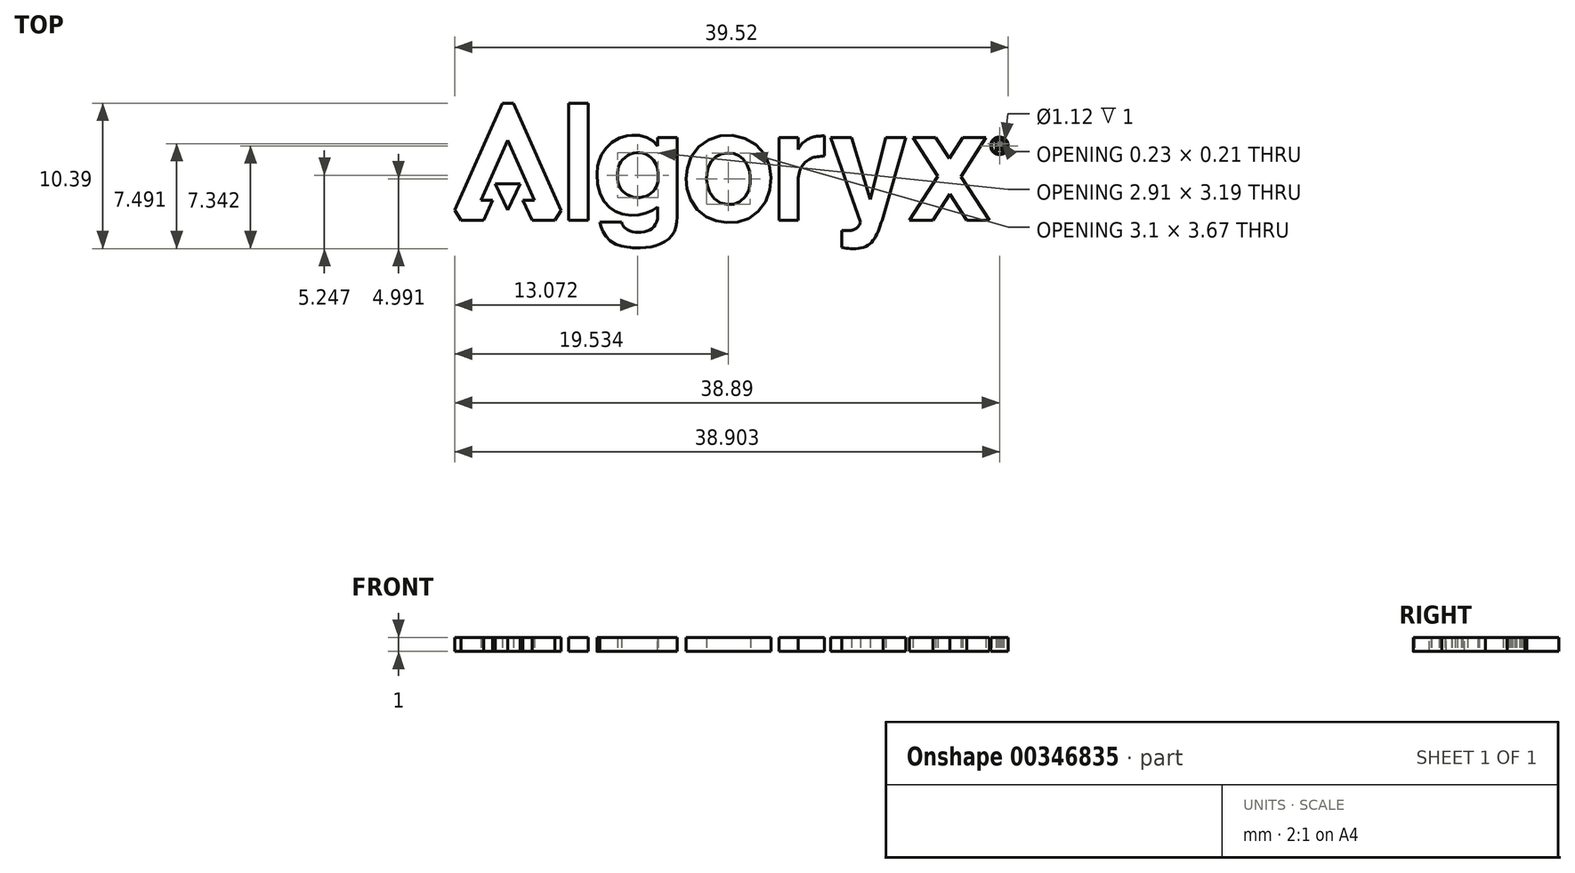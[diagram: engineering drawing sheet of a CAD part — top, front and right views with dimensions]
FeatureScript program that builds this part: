
annotation { "Feature Type Name" : "Feature", "Feature Type Description" : "" }
export const myFeature = defineFeature(function(context is Context, id is Id, definition is map)
    precondition{}
    {
        {
            var Q0;
            Q0=qCreatedBy(makeId("Top.planeOp"),FACE);
            var sketch = newSketch(context, id + "F0", { "sketchPlane" : qUnion([Q0])});
            skLineSegment(sketch, "E0", {"start": v(-19.75, -2.44) * mm, "end": v(-16.35, 5.19) * mm});
            skLineSegment(sketch, "E1", {"start": v(-16.35, 5.19) * mm, "end": v(-15.56, 5.19) * mm});
            skLineSegment(sketch, "E2", {"start": v(-15.56, 5.19) * mm, "end": v(-12.16, -2.46) * mm});
            skLineSegment(sketch, "E3", {"start": v(-12.16, -2.46) * mm, "end": v(-12.6, -3.16) * mm});
            skLineSegment(sketch, "E4", {"start": v(-12.6, -3.16) * mm, "end": v(-14.23, -3.16) * mm});
            skLineSegment(sketch, "E5", {"start": v(-14.23, -3.16) * mm, "end": v(-14.87, -1.75) * mm});
            skLineSegment(sketch, "E6", {"start": v(-14.87, -1.75) * mm, "end": v(-14.04, -1.75) * mm});
            skLineSegment(sketch, "E7", {"start": v(-14.04, -1.75) * mm, "end": v(-15.95, 2.54) * mm});
            skLineSegment(sketch, "E8", {"start": v(-15.95, 2.54) * mm, "end": v(-17.87, -1.75) * mm});
            skLineSegment(sketch, "E9", {"start": v(-17.87, -1.75) * mm, "end": v(-17.03, -1.75) * mm});
            skLineSegment(sketch, "E10", {"start": v(-17.03, -1.75) * mm, "end": v(-17.7, -3.16) * mm});
            skLineSegment(sketch, "E11", {"start": v(-17.7, -3.16) * mm, "end": v(-19.3, -3.16) * mm});
            skLineSegment(sketch, "E12", {"start": v(-19.3, -3.16) * mm, "end": v(-19.75, -2.44) * mm});
            skLineSegment(sketch, "E13", {"start": v(-16.84, -0.58) * mm, "end": v(-15.08, -0.58) * mm});
            skLineSegment(sketch, "E14", {"start": v(-15.08, -0.58) * mm, "end": v(-15.96, -2.45) * mm});
            skLineSegment(sketch, "E15", {"start": v(-15.96, -2.45) * mm, "end": v(-16.84, -0.58) * mm});
            skLineSegment(sketch, "E16.bottom", {"start": v(-11.62, 5.19) * mm, "end": v(-10.2, 5.19) * mm});
            skLineSegment(sketch, "E16.top", {"start": v(-11.62, -3.16) * mm, "end": v(-10.2, -3.16) * mm});
            skLineSegment(sketch, "E16.left", {"start": v(-11.62, 5.19) * mm, "end": v(-11.62, -3.16) * mm});
            skLineSegment(sketch, "E16.right", {"start": v(-10.2, 5.19) * mm, "end": v(-10.2, -3.16) * mm});
            skLineSegment(sketch, "E17", {"start": v(-3.86, 2.72) * mm, "end": v(-3.86, -2.9) * mm});
            skFitSpline(sketch, "E18", {"points": [v(-3.86, -2.9) * mm, v(-4.12, -4.08) * mm, v(-4.9, -4.78) * mm, v(-6, -5.1) * mm, v(-7.01, -5.14) * mm, v(-7.23, -5.12) * mm, v(-8.58, -4.7) * mm, v(-9.33, -3.57) * mm, v(-9.4, -3.29) * mm], "startDerivative": vector(-0.36, -9.23) * mm, "endDerivative": vector(-0.73, 3.2) * mm});
            skLineSegment(sketch, "E19", {"start": v(-9.4, -3.29) * mm, "end": v(-7.85, -3.29) * mm});
            skFitSpline(sketch, "E20", {"points": [v(-7.85, -3.29) * mm, v(-7.73, -3.56) * mm, v(-7.48, -3.82) * mm, v(-6.92, -4.02) * mm, v(-6.2, -4) * mm, v(-5.63, -3.75) * mm, v(-5.3, -3.17) * mm, v(-5.25, -2.56) * mm, v(-5.25, -2.22) * mm], "startDerivative": vector(1.06, -2.97) * mm, "endDerivative": vector(-0.1, 1.67) * mm});
            skFitSpline(sketch, "E21", {"points": [v(-5.25, -2.22) * mm, v(-5.7, -2.51) * mm, v(-6.37, -2.75) * mm, v(-7.11, -2.82) * mm, v(-8, -2.67) * mm, v(-8.59, -2.34) * mm, v(-9.1, -1.8) * mm, v(-9.5, -0.8) * mm, v(-9.57, 0.45) * mm, v(-9.47, 0.98) * mm, v(-9.32, 1.4) * mm, v(-8.9, 2.04) * mm, v(-8.2, 2.6) * mm, v(-7.44, 2.87) * mm, v(-7.07, 2.9) * mm, v(-6.35, 2.84) * mm, v(-5.7, 2.56) * mm, v(-5.25, 2.11) * mm], "startDerivative": vector(-8.31, -6.1) * mm, "endDerivative": vector(7.38, -8.72) * mm});
            skLineSegment(sketch, "E22", {"start": v(-5.25, 2.11) * mm, "end": v(-5.25, 2.72) * mm});
            skLineSegment(sketch, "E23", {"start": v(-5.25, 2.72) * mm, "end": v(-3.86, 2.72) * mm});
            skFitSpline(sketch, "E24", {"points": [v(-8.13, 0) * mm, v(-8.03, -0.65) * mm, v(-7.77, -1.09) * mm, v(-7.56, -1.27) * mm, v(-7.02, -1.5) * mm, v(-6.3, -1.5) * mm, v(-5.8, -1.3) * mm, v(-5.46, -0.94) * mm, v(-5.27, -0.52) * mm, v(-5.22, 0) * mm], "startDerivative": vector(0.32, -5.45) * mm, "endDerivative": vector(0.07, 4.82) * mm});
            skFitSpline(sketch, "E25", {"points": [v(-8.13, 0) * mm, v(-8.06, 0.62) * mm, v(-7.83, 1.08) * mm, v(-7.27, 1.53) * mm, v(-6.6, 1.64) * mm, v(-5.97, 1.47) * mm, v(-5.47, 0.99) * mm, v(-5.3, 0.57) * mm, v(-5.22, 0) * mm], "startDerivative": vector(0.33, 5.16) * mm, "endDerivative": vector(0.08, -5.08) * mm});
            skFitSpline(sketch, "E26", {"points": [v(-1.77, -0.25) * mm, v(-1.7, -0.8) * mm, v(-1.4, -1.4) * mm, v(-0.83, -1.9) * mm, v(-0.21, -2.05) * mm, v(0.38, -1.96) * mm, v(0.91, -1.59) * mm, v(1.24, -1.02) * mm, v(1.36, -0.35) * mm, v(1.33, 0.1) * mm, v(1.2, 0.64) * mm, v(0.82, 1.2) * mm, v(0.55, 1.42) * mm, v(0.22, 1.58) * mm, v(-0.35, 1.63) * mm, v(-0.86, 1.5) * mm, v(-1.27, 1.21) * mm, v(-1.57, 0.77) * mm, v(-1.73, 0.23) * mm, v(-1.77, -0.25) * mm]});
            skFitSpline(sketch, "E27", {"points": [v(-3.23, -0.2) * mm, v(-3.15, -1.03) * mm, v(-2.68, -2.1) * mm, v(-1.9, -2.85) * mm, v(-1.04, -3.24) * mm, v(-0.08, -3.35) * mm, v(0.94, -3.16) * mm, v(1.91, -2.56) * mm, v(2.58, -1.55) * mm, v(2.83, -0.31) * mm, v(2.64, 0.96) * mm, v(1.98, 2.03) * mm, v(0.87, 2.72) * mm, v(-0.42, 2.9) * mm, v(-1.6, 2.6) * mm, v(-2.58, 1.8) * mm, v(-3.11, 0.7) * mm, v(-3.23, -0.2) * mm]});
            skLineSegment(sketch, "E28", {"start": v(3.4, -3.16) * mm, "end": v(3.4, 2.72) * mm});
            skLineSegment(sketch, "E29", {"start": v(3.4, 2.72) * mm, "end": v(4.76, 2.72) * mm});
            skLineSegment(sketch, "E30", {"start": v(4.76, 2.72) * mm, "end": v(4.76, 1.88) * mm});
            skFitSpline(sketch, "E31", {"points": [v(4.76, 1.88) * mm, v(5.08, 2.34) * mm, v(5.64, 2.7) * mm, v(6.11, 2.82) * mm, v(6.63, 2.85) * mm], "startDerivative": vector(1.1, 1.94) * mm, "endDerivative": vector(2.18, 0.06) * mm});
            skLineSegment(sketch, "E32", {"start": v(6.63, 2.85) * mm, "end": v(6.63, 1.42) * mm});
            skLineSegment(sketch, "E33", {"start": v(3.4, -3.16) * mm, "end": v(4.76, -3.16) * mm});
            skLineSegment(sketch, "E34", {"start": v(4.76, -3.16) * mm, "end": v(4.76, -0.48) * mm});
            skFitSpline(sketch, "E35", {"points": [v(4.76, -0.48) * mm, v(4.86, 0.32) * mm, v(5.16, 0.85) * mm, v(5.64, 1.22) * mm, v(6.07, 1.36) * mm, v(6.63, 1.42) * mm], "startDerivative": vector(0.24, 3.63) * mm, "endDerivative": vector(3.01, 0.24) * mm});
            skLineSegment(sketch, "E36", {"start": v(7.08, 2.72) * mm, "end": v(9.21, -3.29) * mm});
            skLineSegment(sketch, "E37", {"start": v(7.08, 2.72) * mm, "end": v(8.59, 2.72) * mm});
            skLineSegment(sketch, "E38", {"start": v(8.59, 2.72) * mm, "end": v(9.92, -1.67) * mm});
            skLineSegment(sketch, "E39", {"start": v(9.92, -1.67) * mm, "end": v(11.03, 2.72) * mm});
            skLineSegment(sketch, "E40", {"start": v(11.03, 2.72) * mm, "end": v(12.47, 2.72) * mm});
            skLineSegment(sketch, "E41", {"start": v(12.47, 2.72) * mm, "end": v(10.82, -2.94) * mm});
            skLineSegment(sketch, "E42", {"start": v(7.88, -3.9) * mm, "end": v(7.88, -5.1) * mm});
            skFitSpline(sketch, "E43", {"points": [v(9.21, -3.29) * mm, v(9.03, -3.64) * mm, v(8.73, -3.85) * mm, v(8.33, -3.92) * mm, v(7.88, -3.9) * mm], "startDerivative": vector(-0.41, -1.67) * mm, "endDerivative": vector(-1.74, 0.13) * mm});
            skFitSpline(sketch, "E44", {"points": [v(7.88, -5.1) * mm, v(8.41, -5.19) * mm, v(9.12, -5.17) * mm, v(9.73, -4.97) * mm, v(10.16, -4.55) * mm, v(10.5, -3.9) * mm, v(10.82, -2.94) * mm], "startDerivative": vector(3.62, -1) * mm, "endDerivative": vector(1.54, 5.02) * mm});
            skLineSegment(sketch, "E45", {"start": v(12.95, 2.72) * mm, "end": v(14.74, -0.02) * mm});
            skLineSegment(sketch, "E46", {"start": v(16.8, -3.17) * mm, "end": v(18.42, -3.17) * mm});
            skLineSegment(sketch, "E47", {"start": v(18.42, -3.17) * mm, "end": v(16.4, -0.05) * mm});
            skLineSegment(sketch, "E48", {"start": v(14.6, 2.72) * mm, "end": v(12.95, 2.72) * mm});
            skLineSegment(sketch, "E49", {"start": v(12.95, 2.72) * mm, "end": v(18.18, 2.72) * mm, "construction": true});
            skLineSegment(sketch, "E50", {"start": v(18.42, -3.17) * mm, "end": v(12.71, -3.17) * mm, "construction": true});
            skLineSegment(sketch, "E51", {"start": v(18.18, 2.72) * mm, "end": v(16.4, -0.05) * mm});
            skLineSegment(sketch, "E52", {"start": v(14.38, -3.17) * mm, "end": v(12.71, -3.17) * mm});
            skLineSegment(sketch, "E53", {"start": v(12.71, -3.17) * mm, "end": v(14.74, -0.02) * mm});
            skLineSegment(sketch, "E54", {"start": v(16.52, 2.72) * mm, "end": v(18.18, 2.72) * mm});
            skLineSegment(sketch, "E55.trimOffspring", {"start": v(15.56, 1.24) * mm, "end": v(14.6, 2.72) * mm});
            skLineSegment(sketch, "E56.trimOffspring", {"start": v(15.56, 1.24) * mm, "end": v(16.52, 2.72) * mm});
            skLineSegment(sketch, "E57.trimOffspring", {"start": v(15.58, -1.3) * mm, "end": v(16.8, -3.17) * mm});
            skLineSegment(sketch, "E58.trimOffspring", {"start": v(15.58, -1.3) * mm, "end": v(14.38, -3.17) * mm});
            skCircle(sketch, "E59", {"center": v(19.14, 2.14) * mm, "radius": 0.56 * mm});
            skPoint(sketch, "E59.first.point", {"position": v(19.13, 2.7) * mm});
            skPoint(sketch, "E59.second.point", {"position": v(18.58, 2.12) * mm});
            skPoint(sketch, "E59.third.point", {"position": v(19.51, 1.73) * mm});
            skCircle(sketch, "E60", {"center": v(19.14, 2.14) * mm, "radius": 0.63 * mm});
            skLineSegment(sketch, "E61", {"start": v(18.89, 1.76) * mm, "end": v(18.89, 2.53) * mm});
            skLineSegment(sketch, "E62", {"start": v(18.89, 2.53) * mm, "end": v(19.27, 2.53) * mm});
            skLineSegment(sketch, "E63", {"start": v(18.89, 1.76) * mm, "end": v(19.04, 1.76) * mm});
            skLineSegment(sketch, "E64", {"start": v(19.04, 1.76) * mm, "end": v(19.04, 2.06) * mm});
            skLineSegment(sketch, "E65", {"start": v(19.04, 2.06) * mm, "end": v(19.15, 2.06) * mm});
            skLineSegment(sketch, "E66", {"start": v(19.15, 2.06) * mm, "end": v(19.26, 1.76) * mm});
            skLineSegment(sketch, "E67", {"start": v(19.26, 1.76) * mm, "end": v(19.42, 1.76) * mm});
            skLineSegment(sketch, "E68", {"start": v(19.42, 1.76) * mm, "end": v(19.3, 2.08) * mm});
            skFitSpline(sketch, "E69", {"points": [v(19.3, 2.08) * mm, v(19.37, 2.14) * mm, v(19.42, 2.28) * mm, v(19.38, 2.44) * mm, v(19.27, 2.53) * mm], "startDerivative": vector(0.36, 0.27) * mm, "endDerivative": vector(-0.55, 0.17) * mm});
            skLineSegment(sketch, "E70", {"start": v(19.04, 2.19) * mm, "end": v(19.04, 2.4) * mm});
            skLineSegment(sketch, "E71", {"start": v(19.04, 2.19) * mm, "end": v(19.04, 2.06) * mm, "construction": true});
            skFitSpline(sketch, "E72", {"points": [v(19.04, 2.4) * mm, v(19.18, 2.4) * mm, v(19.25, 2.35) * mm, v(19.27, 2.29) * mm, v(19.25, 2.22) * mm, v(19.18, 2.19) * mm, v(19.04, 2.19) * mm], "startDerivative": vector(0.81, 0.02) * mm, "endDerivative": vector(-0.74, 0.05) * mm});
            skSolve(sketch);
        }
        {
            var Q0;
            Q0 = qSketchRegion(id + "F0", true);
            var Q1;
            Q1=makeQuery(id+"F0.imprint","IMPRINT",FACE,{"disambiguationData":[TD([[makeQuery(id+"F0.imprint","IMPRINT",EDGE,{"derivedFrom":sQuery(id+"F0.wireOp",EDGE,"E61")}),-1.0]])]});
            extrude(context, id + "F1", {"entities" : qUnion([Q0, Q1]), "depth" : 1 * mm});
        }
    });
